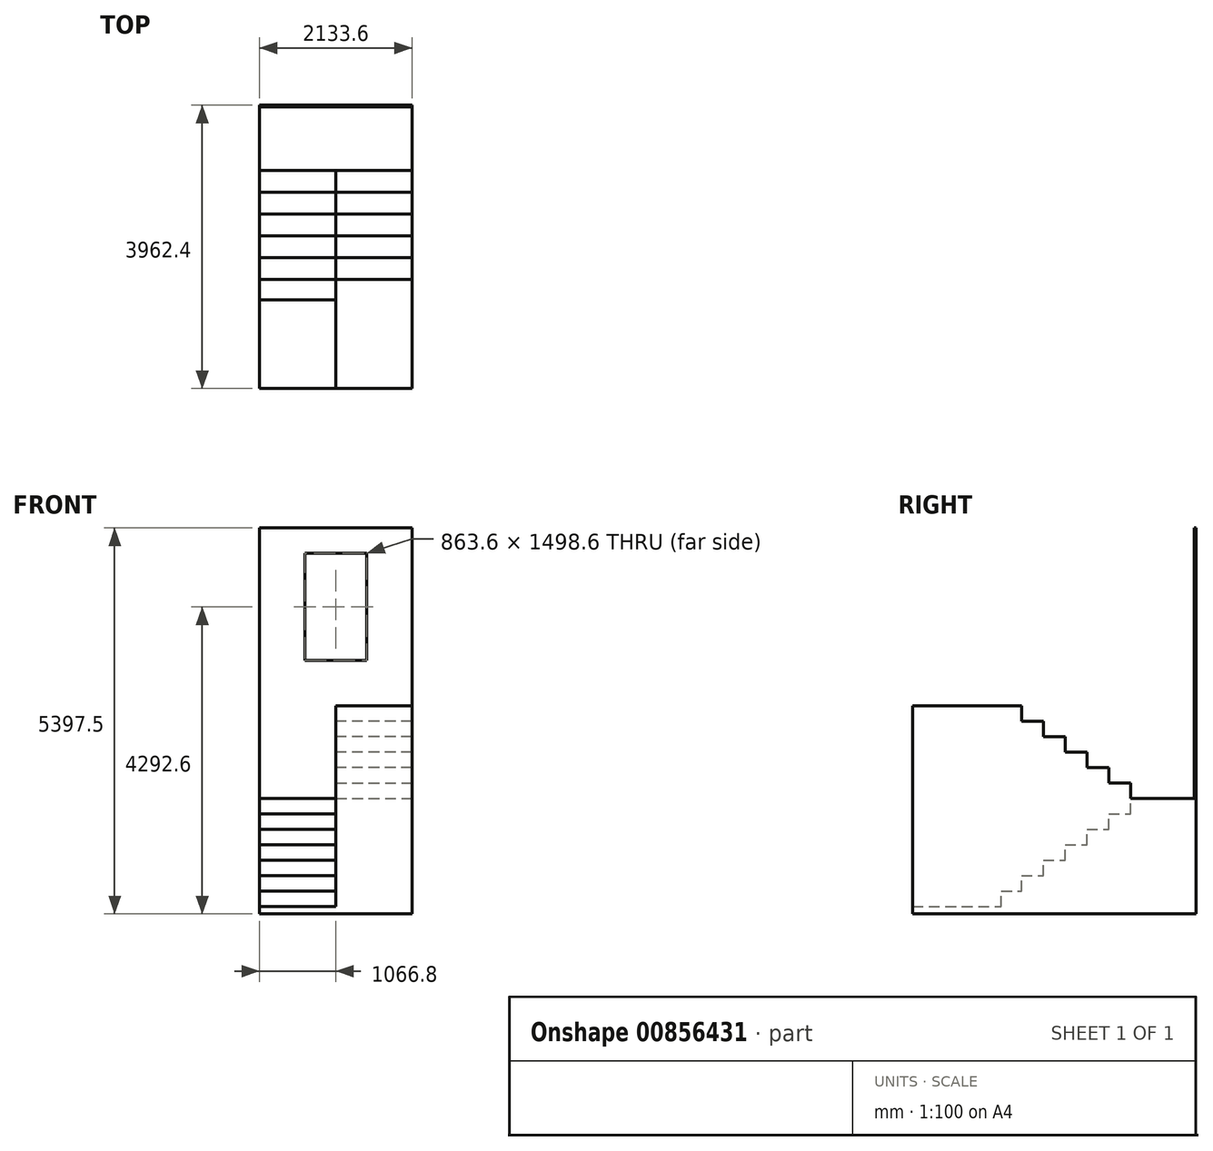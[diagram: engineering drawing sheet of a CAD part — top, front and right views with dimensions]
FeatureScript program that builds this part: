
annotation { "Feature Type Name" : "Feature", "Feature Type Description" : "" }
export const myFeature = defineFeature(function(context is Context, id is Id, definition is map)
    precondition{}
    {
        {
            var Q0;
            Q0=qCreatedBy(makeId("Top.planeOp"),FACE);
            var sketch = newSketch(context, id + "F0", { "sketchPlane" : qUnion([Q0])});
            skLineSegment(sketch, "E0.bottom", {"start": v(1066.8, -1358.9) * mm, "end": v(-1066.8, -1358.9) * mm});
            skLineSegment(sketch, "E0.top", {"start": v(1066.8, 1358.9) * mm, "end": v(-1066.8, 1358.9) * mm});
            skLineSegment(sketch, "E0.left", {"start": v(1066.8, -1358.9) * mm, "end": v(1066.8, 1358.9) * mm});
            skLineSegment(sketch, "E0.right", {"start": v(-1066.8, -1358.9) * mm, "end": v(-1066.8, 1358.9) * mm});
            skPoint(sketch, "E0.middle", {"position": v(0, 0) * mm});
            skSolve(sketch);
        }
        {
            var Q0;
            Q0=makeQuery(id+"F0.imprint","IMPRINT",FACE,{"disambiguationData":[TD([[makeQuery(id+"F0.imprint","IMPRINT",EDGE,{"derivedFrom":sQuery(id+"F0.wireOp",EDGE,"E0.bottom")}),-1.0]])]});
            extrude(context, id + "F1", {"entities" : qUnion([Q0]), "depth" : 38.1 * mm, "offsetDistance" : 25.4 * mm});
        }
        {
            var Q0;
            Q0=makeQuery(id+"F1.opExtrude","SWEPT_FACE",FACE,{"disambiguationData":[OSD([sQuery(id+"F0.wireOp",EDGE,"E0.top")])]});
            var sketch = newSketch(context, id + "F2", { "sketchPlane" : qUnion([Q0])});
            skLineSegment(sketch, "E1.top", {"start": v(-1066.8, 3822.7) * mm, "end": v(1066.8, 3822.7) * mm});
            skLineSegment(sketch, "E1.left", {"start": v(-1066.8, 38.1) * mm, "end": v(-1066.8, 3822.7) * mm});
            skLineSegment(sketch, "E1.right", {"start": v(1066.8, 38.1) * mm, "end": v(1066.8, 3822.7) * mm});
            skLineSegment(sketch, "E2.top", {"start": v(1066.8, 0) * mm, "end": v(-1066.8, 0) * mm});
            skLineSegment(sketch, "E2.left", {"start": v(1066.8, 38.1) * mm, "end": v(1066.8, 0) * mm});
            skLineSegment(sketch, "E2.right", {"start": v(-1066.8, 38.1) * mm, "end": v(-1066.8, 0) * mm});
            skSolve(sketch);
        }
        {
            var Q0;
            Q0 = qSketchRegion(id + "F2", true);
            extrude(context, id + "F3", {"entities" : qUnion([Q0]), "operationType" : NewBodyOperationType.ADD, "depth" : 25.4 * mm, "offsetDistance" : 25.4 * mm});
        }
        {
            var Q0;
            Q0=makeQuery(id+"F3.opExtrude","CAP_FACE",FACE,{"disambiguationData":[OSD([sQuery(id+"F2.wireOp",EDGE,"E1.top"),sQuery(id+"F2.wireOp",EDGE,"E1.left"),sQuery(id+"F2.wireOp",EDGE,"E1.right"),sQuery(id+"F2.wireOp",EDGE,"E2.top"),sQuery(id+"F2.wireOp",EDGE,"E2.left"),sQuery(id+"F2.wireOp",EDGE,"E2.right")])],"isStart":true});
            var sketch = newSketch(context, id + "F4", { "sketchPlane" : qUnion([Q0])});
            skLineSegment(sketch, "E3.bottom", {"start": v(431.8, 1968.5) * mm, "end": v(-431.8, 1968.5) * mm});
            skLineSegment(sketch, "E3.top", {"start": v(431.8, 3467.1) * mm, "end": v(-431.8, 3467.1) * mm});
            skLineSegment(sketch, "E3.left", {"start": v(431.8, 1968.5) * mm, "end": v(431.8, 3467.1) * mm});
            skLineSegment(sketch, "E3.right", {"start": v(-431.8, 1968.5) * mm, "end": v(-431.8, 3467.1) * mm});
            skPoint(sketch, "E3.middle", {"position": v(0, 2717.8) * mm});
            skSolve(sketch);
        }
        {
            var Q0;
            Q0=makeQuery(id+"F4.imprint","IMPRINT",FACE,{"disambiguationData":[TD([[makeQuery(id+"F4.imprint","IMPRINT",EDGE,{"derivedFrom":sQuery(id+"F4.wireOp",EDGE,"E3.bottom")}),-1.0]])]});
            extrude(context, id + "F5", {"entities" : qUnion([Q0]), "operationType" : NewBodyOperationType.REMOVE, "oppositeDirection" : true, "depth" : 50.8 * mm, "offsetDistance" : 25.4 * mm});
        }
        {
            var Q0;
            Q0=makeQuery(id+"F1.opExtrude","CAP_FACE",FACE,{"disambiguationData":[OSD([sQuery(id+"F0.wireOp",EDGE,"E0.bottom"),sQuery(id+"F0.wireOp",EDGE,"E0.top"),sQuery(id+"F0.wireOp",EDGE,"E0.left"),sQuery(id+"F0.wireOp",EDGE,"E0.right")])],"isStart":false});
            var sketch = newSketch(context, id + "F6", { "sketchPlane" : qUnion([Q0])});
            skLineSegment(sketch, "E4", {"start": v(0, 469.9) * mm, "end": v(0, -1358.9) * mm});
            skLineSegment(sketch, "E5", {"start": v(0, 469.9) * mm, "end": v(-1066.8, 469.9) * mm});
            skPoint(sketch, "E6.start.orphan", {"position": v(0, 1358.9) * mm});
            skLineSegment(sketch, "E7", {"start": v(-1066.8, 469.9) * mm, "end": v(-1066.8, 165.1) * mm});
            skLineSegment(sketch, "E8", {"start": v(-1066.8, 165.1) * mm, "end": v(0, 165.1) * mm});
            skLineSegment(sketch, "E9", {"start": v(-1066.8, 165.1) * mm, "end": v(-1066.8, -139.7) * mm});
            skLineSegment(sketch, "E10", {"start": v(-1066.8, -139.7) * mm, "end": v(0, -139.7) * mm});
            skLineSegment(sketch, "E11", {"start": v(-1066.8, -139.7) * mm, "end": v(-1066.8, -444.5) * mm});
            skLineSegment(sketch, "E12", {"start": v(-1066.8, -444.5) * mm, "end": v(0, -444.5) * mm});
            skLineSegment(sketch, "E13", {"start": v(-1066.8, -444.5) * mm, "end": v(-1066.8, -749.3) * mm});
            skLineSegment(sketch, "E14", {"start": v(-1066.8, -749.3) * mm, "end": v(0, -749.3) * mm});
            skLineSegment(sketch, "E15", {"start": v(-1066.8, -749.3) * mm, "end": v(-1066.8, -1054.1) * mm});
            skLineSegment(sketch, "E16", {"start": v(-1066.8, -1054.1) * mm, "end": v(0, -1054.1) * mm});
            skSolve(sketch);
        }
        {
            var Q0;
            Q0=makeQuery(id+"F3.boolean.opBoolean","MERGE",FACE,{"derivedFrom":[makeQuery(id+"F1.opExtrude","CAP_FACE",FACE,{"disambiguationData":[OSD([sQuery(id+"F0.wireOp",EDGE,"E0.bottom"),sQuery(id+"F0.wireOp",EDGE,"E0.top"),sQuery(id+"F0.wireOp",EDGE,"E0.left"),sQuery(id+"F0.wireOp",EDGE,"E0.right")])],"isStart":true}),makeQuery(id+"F3.opExtrude","SWEPT_FACE",FACE,{"disambiguationData":[OSD([sQuery(id+"F2.wireOp",EDGE,"E2.top")])]})]});
            extrude(context, id + "F7", {"entities" : qUnion([Q0]), "operationType" : NewBodyOperationType.ADD, "depth" : 1574.8 * mm, "offsetDistance" : 25.4 * mm});
        }
        {
            var Q0;
            {var subQ3=sQuery(id+"F6.wireOp",EDGE,"E16");Q0=makeQuery(id+"F6.imprint","IMPRINT",FACE,{"disambiguationData":[TD([[makeQuery(id+"F6.imprint","IMPRINT",EDGE,{"derivedFrom":subQ3}),-1.0]])]});}
            extrude(context, id + "F8", {"entities" : qUnion([Q0]), "operationType" : NewBodyOperationType.REMOVE, "oppositeDirection" : true, "depth" : 1295.4 * mm, "offsetDistance" : 25.4 * mm});
        }
        {
            var Q0;
            {var subQ0=sQuery(id+"F6.wireOp",EDGE,"E14");Q0=makeQuery(id+"F6.imprint","IMPRINT",FACE,{"disambiguationData":[TD([[makeQuery(id+"F6.imprint","IMPRINT",EDGE,{"derivedFrom":subQ0}),-1.0]])]});}
            extrude(context, id + "F9", {"entities" : qUnion([Q0]), "operationType" : NewBodyOperationType.REMOVE, "oppositeDirection" : true, "depth" : 1079.5 * mm, "offsetDistance" : 25.4 * mm});
        }
        {
            var Q0;
            {var subQ0=sQuery(id+"F6.wireOp",EDGE,"E12");Q0=makeQuery(id+"F6.imprint","IMPRINT",FACE,{"disambiguationData":[TD([[makeQuery(id+"F6.imprint","IMPRINT",EDGE,{"derivedFrom":subQ0}),-1.0]])]});}
            extrude(context, id + "F10", {"entities" : qUnion([Q0]), "operationType" : NewBodyOperationType.REMOVE, "oppositeDirection" : true, "depth" : 863.6 * mm, "offsetDistance" : 25.4 * mm});
        }
        {
            var Q0;
            {var subQ0=sQuery(id+"F6.wireOp",EDGE,"E10");Q0=makeQuery(id+"F6.imprint","IMPRINT",FACE,{"disambiguationData":[TD([[makeQuery(id+"F6.imprint","IMPRINT",EDGE,{"derivedFrom":subQ0}),-1.0]])]});}
            extrude(context, id + "F11", {"entities" : qUnion([Q0]), "operationType" : NewBodyOperationType.REMOVE, "oppositeDirection" : true, "depth" : 647.7 * mm, "offsetDistance" : 25.4 * mm});
        }
        {
            var Q0;
            {var subQ0=sQuery(id+"F6.wireOp",EDGE,"E8");Q0=makeQuery(id+"F6.imprint","IMPRINT",FACE,{"disambiguationData":[TD([[makeQuery(id+"F6.imprint","IMPRINT",EDGE,{"derivedFrom":subQ0}),-1.0]])]});}
            extrude(context, id + "F12", {"entities" : qUnion([Q0]), "operationType" : NewBodyOperationType.REMOVE, "oppositeDirection" : true, "depth" : 431.8 * mm, "offsetDistance" : 25.4 * mm});
        }
        {
            var Q0;
            {var subQ0=sQuery(id+"F6.wireOp",EDGE,"E5");Q0=makeQuery(id+"F6.imprint","IMPRINT",FACE,{"disambiguationData":[TD([[makeQuery(id+"F6.imprint","IMPRINT",EDGE,{"derivedFrom":subQ0}),1.0]])]});}
            extrude(context, id + "F13", {"entities" : qUnion([Q0]), "operationType" : NewBodyOperationType.REMOVE, "oppositeDirection" : true, "depth" : 215.9 * mm, "offsetDistance" : 25.4 * mm});
        }
        {
            var Q0;
            Q0=makeQuery(id+"F1.opExtrude","CAP_FACE",FACE,{"disambiguationData":[OSD([sQuery(id+"F0.wireOp",EDGE,"E0.bottom"),sQuery(id+"F0.wireOp",EDGE,"E0.top"),sQuery(id+"F0.wireOp",EDGE,"E0.left"),sQuery(id+"F0.wireOp",EDGE,"E0.right")])],"isStart":false});
            var sketch = newSketch(context, id + "F14", { "sketchPlane" : qUnion([Q0])});
            skLineSegment(sketch, "E17", {"start": v(0, 469.9) * mm, "end": v(1066.8, 469.9) * mm});
            skLineSegment(sketch, "E18", {"start": v(1066.8, 469.9) * mm, "end": v(1066.8, 165.1) * mm});
            skLineSegment(sketch, "E19", {"start": v(1066.8, 165.1) * mm, "end": v(1066.8, -139.7) * mm});
            skLineSegment(sketch, "E20", {"start": v(1066.8, -139.7) * mm, "end": v(1066.8, -444.5) * mm});
            skLineSegment(sketch, "E21", {"start": v(1066.8, -444.5) * mm, "end": v(1066.8, -749.3) * mm});
            skLineSegment(sketch, "E22", {"start": v(1066.8, -749.3) * mm, "end": v(1066.8, -1054.1) * mm});
            skLineSegment(sketch, "E23", {"start": v(1066.8, 165.1) * mm, "end": v(0, 165.1) * mm});
            skLineSegment(sketch, "E24", {"start": v(1066.8, -139.7) * mm, "end": v(0, -139.7) * mm});
            skLineSegment(sketch, "E25", {"start": v(1066.8, -444.5) * mm, "end": v(0, -444.5) * mm});
            skLineSegment(sketch, "E26", {"start": v(1066.8, -749.3) * mm, "end": v(0, -749.3) * mm});
            skLineSegment(sketch, "E27", {"start": v(1066.8, -1054.1) * mm, "end": v(0, -1054.1) * mm});
            skSolve(sketch);
        }
        {
            var Q0;
            {var subQ0=sQuery(id+"F14.wireOp",EDGE,"E17");Q0=makeQuery(id+"F14.imprint","IMPRINT",FACE,{"disambiguationData":[TD([[makeQuery(id+"F14.imprint","IMPRINT",EDGE,{"derivedFrom":subQ0}),-1.0]])]});}
            extrude(context, id + "F15", {"entities" : qUnion([Q0]), "operationType" : NewBodyOperationType.ADD, "depth" : 215.9 * mm, "offsetDistance" : 25.4 * mm});
        }
        {
            var Q0;
            Q0=makeQuery(id+"F14.imprint","IMPRINT",FACE,{"disambiguationData":[TD([[makeQuery(id+"F14.imprint","IMPRINT",EDGE,{"derivedFrom":sQuery(id+"F14.wireOp",EDGE,"E19")}),1.0]])]});
            extrude(context, id + "F16", {"entities" : qUnion([Q0]), "operationType" : NewBodyOperationType.ADD, "depth" : 431.8 * mm, "offsetDistance" : 25.4 * mm});
        }
        {
            var Q0;
            Q0=makeQuery(id+"F14.imprint","IMPRINT",FACE,{"disambiguationData":[TD([[makeQuery(id+"F14.imprint","IMPRINT",EDGE,{"derivedFrom":sQuery(id+"F14.wireOp",EDGE,"E20")}),1.0]])]});
            extrude(context, id + "F17", {"entities" : qUnion([Q0]), "operationType" : NewBodyOperationType.ADD, "depth" : 647.7 * mm, "offsetDistance" : 25.4 * mm});
        }
        {
            var Q0;
            Q0=makeQuery(id+"F14.imprint","IMPRINT",FACE,{"disambiguationData":[TD([[makeQuery(id+"F14.imprint","IMPRINT",EDGE,{"derivedFrom":sQuery(id+"F14.wireOp",EDGE,"E21")}),1.0]])]});
            extrude(context, id + "F18", {"entities" : qUnion([Q0]), "operationType" : NewBodyOperationType.ADD, "depth" : 863.6 * mm, "offsetDistance" : 25.4 * mm});
        }
        {
            var Q0;
            Q0=makeQuery(id+"F14.imprint","IMPRINT",FACE,{"disambiguationData":[TD([[makeQuery(id+"F14.imprint","IMPRINT",EDGE,{"derivedFrom":sQuery(id+"F14.wireOp",EDGE,"E22")}),1.0]])]});
            extrude(context, id + "F19", {"entities" : qUnion([Q0]), "operationType" : NewBodyOperationType.ADD, "depth" : 1079.5 * mm, "offsetDistance" : 25.4 * mm});
        }
        {
            var Q0;
            {var subQ2=sQuery(id+"F0.wireOp",EDGE,"E0.left");var subQ3=sQuery(id+"F0.wireOp",EDGE,"E0.bottom");Q0=makeQuery(id+"F15.boolean.opBoolean","SPLIT",FACE,{"disambiguationData":[TD([makeQuery(id+"F1.opExtrude","SWEPT_FACE",FACE,{"disambiguationData":[OSD([subQ3])]})])],"derivedFrom":makeQuery(id+"F1.opExtrude","CAP_FACE",FACE,{"disambiguationData":[OSD([subQ3,sQuery(id+"F0.wireOp",EDGE,"E0.top"),subQ2,sQuery(id+"F0.wireOp",EDGE,"E0.right")])],"isStart":false})});}
            extrude(context, id + "F20", {"entities" : qUnion([Q0]), "operationType" : NewBodyOperationType.ADD, "depth" : 1295.4 * mm, "offsetDistance" : 25.4 * mm});
        }
        {
            var Q0;
            {var subQ0=sQuery(id+"F0.wireOp",EDGE,"E0.bottom");Q0=makeQuery(id+"F20.boolean.opBoolean","MERGE",FACE,{"derivedFrom":[makeQuery(id+"F7.boolean.opBoolean","MERGE",FACE,{"derivedFrom":[makeQuery(id+"F1.opExtrude","SWEPT_FACE",FACE,{"disambiguationData":[OSD([subQ0])]}),makeQuery(id+"F7.opExtrude","SWEPT_FACE",FACE,{"disambiguationData":[OSD([subQ0])]})]}),makeQuery(id+"F20.opExtrude","SWEPT_FACE",FACE,{"disambiguationData":[OSD([subQ0])]})]});}
            extrude(context, id + "F21", {"entities" : qUnion([Q0]), "operationType" : NewBodyOperationType.ADD, "depth" : 1219.2 * mm, "offsetDistance" : 25.4 * mm});
        }
        {
            var Q0;
            {var subQ0=sQuery(id+"F0.wireOp",EDGE,"E0.bottom");Q0=makeQuery(id+"F21.boolean.opBoolean","MERGE",FACE,{"derivedFrom":[makeQuery(id+"F8.boolean.opBoolean","COPY",FACE,{"derivedFrom":makeQuery(id+"F8.opExtrude","CAP_FACE",FACE,{"disambiguationData":[OSD([subQ0,sQuery(id+"F0.wireOp",EDGE,"E0.right"),sQuery(id+"F6.wireOp",EDGE,"E4"),sQuery(id+"F6.wireOp",EDGE,"E16")])],"isStart":false})}),makeQuery(id+"F21.opExtrude","SWEPT_FACE",FACE,{"disambiguationData":[OSD([subQ0]),TDD([makeQuery(id+"F8.boolean.opBoolean","COPY",EDGE,{"derivedFrom":makeQuery(id+"F8.opExtrude","CAP_EDGE",EDGE,{"disambiguationData":[OSD([subQ0])],"isStart":false})})])]})]});}
            var sketch = newSketch(context, id + "F22", { "sketchPlane" : qUnion([Q0])});
            skLineSegment(sketch, "E28", {"start": v(0, -1336.72) * mm, "end": v(-1066.8, -1336.72) * mm});
            skSolve(sketch);
        }
        {
            var Q0;
            {var subQ0=sQuery(id+"F22.wireOp",EDGE,"E28");Q0=makeQuery(id+"F22.imprint","IMPRINT",FACE,{"disambiguationData":[TD([[makeQuery(id+"F22.imprint","IMPRINT",EDGE,{"derivedFrom":subQ0}),1.0]])]});}
            extrude(context, id + "F23", {"entities" : qUnion([Q0]), "operationType" : NewBodyOperationType.REMOVE, "oppositeDirection" : true, "depth" : 215.9 * mm, "offsetDistance" : 25.4 * mm});
        }
    });
